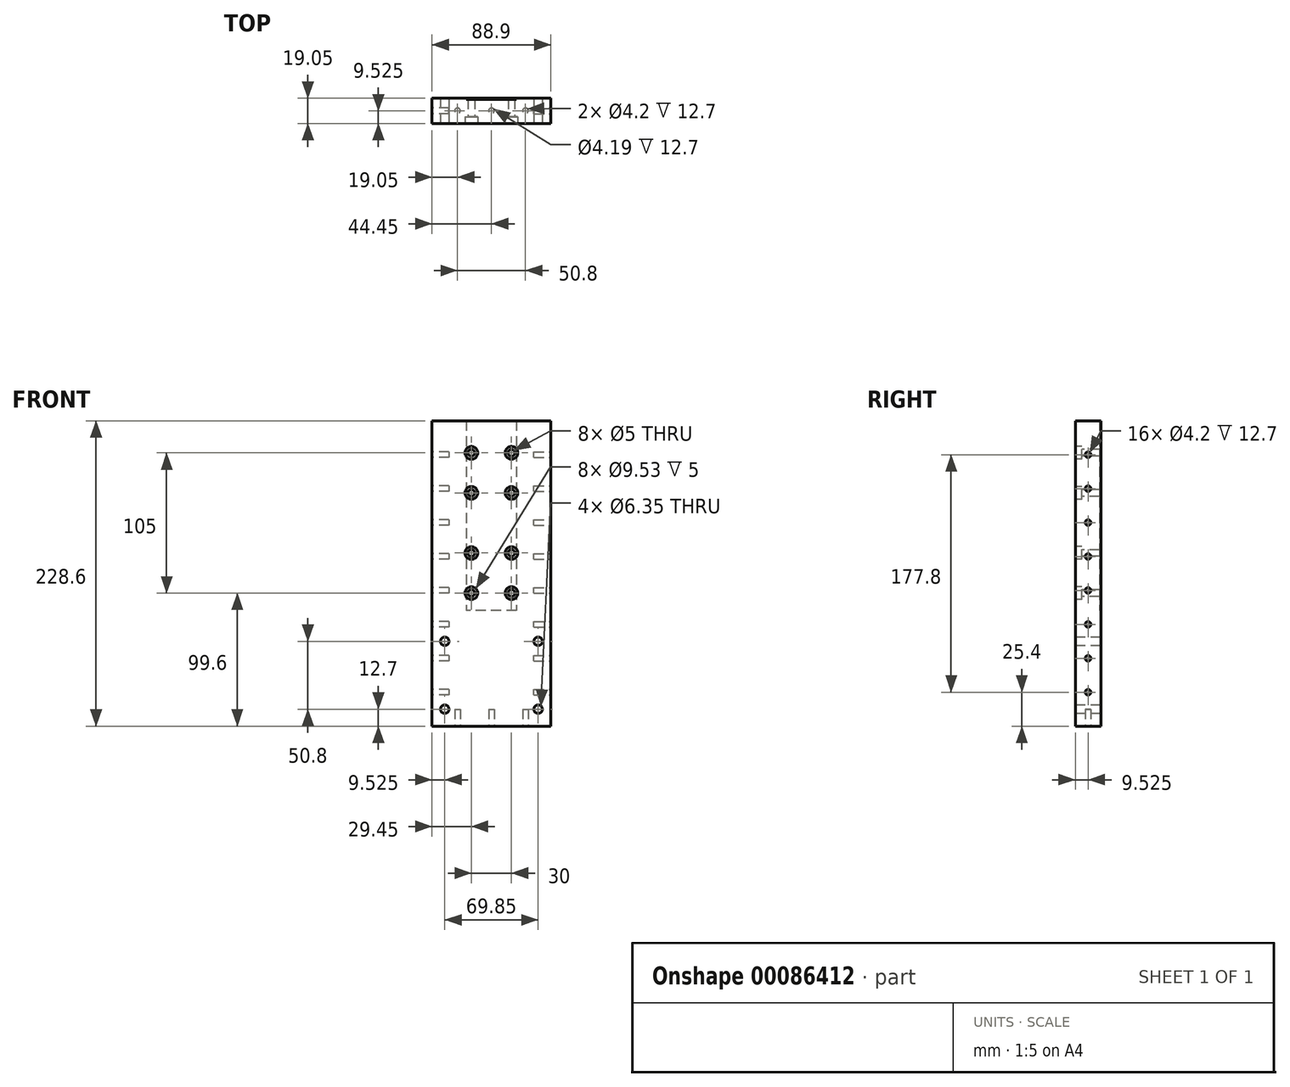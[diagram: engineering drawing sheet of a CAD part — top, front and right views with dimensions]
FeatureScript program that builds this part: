
annotation { "Feature Type Name" : "Feature", "Feature Type Description" : "" }
export const myFeature = defineFeature(function(context is Context, id is Id, definition is map)
    precondition{}
    {
        {
            var Q0;
            Q0=qCreatedBy(makeId("Front.planeOp"),FACE);
            var sketch = newSketch(context, id + "F0", { "sketchPlane" : qUnion([Q0])});
            skLineSegment(sketch, "E0.bottom", {"start": v(44.45, -114.3) * mm, "end": v(-44.45, -114.3) * mm});
            skLineSegment(sketch, "E0.top", {"start": v(44.45, 114.3) * mm, "end": v(-44.45, 114.3) * mm});
            skLineSegment(sketch, "E0.left", {"start": v(44.45, -114.3) * mm, "end": v(44.45, 114.3) * mm});
            skLineSegment(sketch, "E0.right", {"start": v(-44.45, -114.3) * mm, "end": v(-44.45, 114.3) * mm});
            skPoint(sketch, "E0.middle", {"position": v(0, 0) * mm});
            skSolve(sketch);
        }
        {
            var Q0;
            Q0=makeQuery(id+"F0.imprint","IMPRINT",FACE,{"disambiguationData":[TD([[makeQuery(id+"F0.imprint","IMPRINT",EDGE,{"derivedFrom":sQuery(id+"F0.wireOp",EDGE,"E0.bottom")}),-1.0]])]});
            extrude(context, id + "F1", {"entities" : qUnion([Q0]), "oppositeDirection" : true, "depth" : 19.05 * mm});
        }
        {
            var Q0;
            Q0=makeQuery(id+"F1.opExtrude","CAP_FACE",FACE,{"disambiguationData":[OSD([sQuery(id+"F0.wireOp",EDGE,"E0.bottom"),sQuery(id+"F0.wireOp",EDGE,"E0.top"),sQuery(id+"F0.wireOp",EDGE,"E0.left"),sQuery(id+"F0.wireOp",EDGE,"E0.right")])],"isStart":true});
            var sketch = newSketch(context, id + "F2", { "sketchPlane" : qUnion([Q0])});
            skLineSegment(sketch, "E1", {"start": v(0, 118.6) * mm, "end": v(0, -123.74) * mm, "construction": true});
            skPoint(sketch, "E1.endSnap0", {"position": v(0, -114.3) * mm});
            skLineSegment(sketch, "E2", {"start": v(-15, 118.28) * mm, "end": v(-15, -54.2) * mm, "construction": true});
            skLineSegment(sketch, "E3", {"start": v(15, 118.28) * mm, "end": v(15, -54.75) * mm, "construction": true});
            skLineSegment(sketch, "E4", {"start": v(-47, 90.3) * mm, "end": v(45.55, 90.3) * mm});
            skLineSegment(sketch, "E5", {"start": v(-45.9, 60.3) * mm, "end": v(47.2, 60.3) * mm});
            skLineSegment(sketch, "E6", {"start": v(-45.9, 15.3) * mm, "end": v(49.67, 15.3) * mm});
            skLineSegment(sketch, "E7", {"start": v(-46.73, -14.7) * mm, "end": v(49.4, -14.7) * mm});
            skCircle(sketch, "E8", {"center": v(-15, 90.3) * mm, "radius": 2.5 * mm});
            skCircle(sketch, "E9", {"center": v(15, 90.3) * mm, "radius": 2.5 * mm});
            skCircle(sketch, "E10", {"center": v(-15, 60.3) * mm, "radius": 2.5 * mm});
            skCircle(sketch, "E11", {"center": v(15, 60.3) * mm, "radius": 2.5 * mm});
            skCircle(sketch, "E12", {"center": v(-15, 15.3) * mm, "radius": 2.5 * mm});
            skCircle(sketch, "E13", {"center": v(15, 15.3) * mm, "radius": 2.5 * mm});
            skCircle(sketch, "E14", {"center": v(-15, -14.7) * mm, "radius": 2.5 * mm});
            skCircle(sketch, "E15", {"center": v(15, -14.7) * mm, "radius": 2.5 * mm});
            skSolve(sketch);
        }
        {
            var Q0;
            Q0 = qSketchRegion(id + "F2", true);
            extrude(context, id + "F3", {"entities" : qUnion([Q0]), "operationType" : NewBodyOperationType.REMOVE, "endBound" : BoundingType.THROUGH_ALL, "oppositeDirection" : true, "depth" : 25.4 * mm});
        }
        {
            var Q0;
            Q0=makeQuery(id+"F1.opExtrude","CAP_FACE",FACE,{"disambiguationData":[OSD([sQuery(id+"F0.wireOp",EDGE,"E0.bottom"),sQuery(id+"F0.wireOp",EDGE,"E0.top"),sQuery(id+"F0.wireOp",EDGE,"E0.left"),sQuery(id+"F0.wireOp",EDGE,"E0.right")])],"isStart":true});
            var sketch = newSketch(context, id + "F4", { "sketchPlane" : qUnion([Q0])});
            skCircle(sketch, "E16", {"center": v(-15, -14.7) * mm, "radius": 4.76 * mm});
            skCircle(sketch, "E17", {"center": v(15, -14.7) * mm, "radius": 4.76 * mm});
            skCircle(sketch, "E18", {"center": v(15, 15.3) * mm, "radius": 4.76 * mm});
            skCircle(sketch, "E19", {"center": v(-15, 15.3) * mm, "radius": 4.76 * mm});
            skCircle(sketch, "E20", {"center": v(-15, 60.3) * mm, "radius": 4.76 * mm});
            skCircle(sketch, "E21", {"center": v(15, 60.3) * mm, "radius": 4.76 * mm});
            skCircle(sketch, "E22", {"center": v(-15, 90.3) * mm, "radius": 4.76 * mm});
            skCircle(sketch, "E23", {"center": v(15, 90.3) * mm, "radius": 4.76 * mm});
            skSolve(sketch);
        }
        {
            var Q0;
            Q0 = qSketchRegion(id + "F4", true);
            extrude(context, id + "F5", {"entities" : qUnion([Q0]), "operationType" : NewBodyOperationType.REMOVE, "oppositeDirection" : true, "depth" : 5 * mm});
        }
        {
            var Q0;
            Q0=makeQuery(id+"F1.opExtrude","SWEPT_FACE",FACE,{"disambiguationData":[OSD([sQuery(id+"F0.wireOp",EDGE,"E0.right")])]});
            var sketch = newSketch(context, id + "F6", { "sketchPlane" : qUnion([Q0])});
            skLineSegment(sketch, "E24", {"start": v(-9.53, -118.31) * mm, "end": v(-9.53, 120.01) * mm, "construction": true});
            skPoint(sketch, "E24.startSnap0", {"position": v(-9.53, -114.3) * mm});
            skCircle(sketch, "E25", {"center": v(-9.53, 88.9) * mm, "radius": 2.1 * mm});
            skCircle(sketch, "E26", {"center": v(-9.53, 63.5) * mm, "radius": 2.1 * mm});
            skCircle(sketch, "E27", {"center": v(-9.53, 38.1) * mm, "radius": 2.1 * mm});
            skCircle(sketch, "E28", {"center": v(-9.53, 12.7) * mm, "radius": 2.1 * mm});
            skCircle(sketch, "E29", {"center": v(-9.53, -12.7) * mm, "radius": 2.1 * mm});
            skCircle(sketch, "E30", {"center": v(-9.53, -38.1) * mm, "radius": 2.1 * mm});
            skCircle(sketch, "E31", {"center": v(-9.52, -63.5) * mm, "radius": 2.1 * mm});
            skCircle(sketch, "E32", {"center": v(-9.52, -88.9) * mm, "radius": 2.1 * mm});
            skSolve(sketch);
        }
        {
            var Q0;
            Q0 = qSketchRegion(id + "F6", true);
            extrude(context, id + "F7", {"entities" : qUnion([Q0]), "operationType" : NewBodyOperationType.REMOVE, "oppositeDirection" : true, "depth" : 12.7 * mm});
        }
        {
            var Q0;
            Q0=makeQuery(id+"F1.opExtrude","SWEPT_FACE",FACE,{"disambiguationData":[OSD([sQuery(id+"F0.wireOp",EDGE,"E0.left")])]});
            var sketch = newSketch(context, id + "F8", { "sketchPlane" : qUnion([Q0])});
            skLineSegment(sketch, "E33", {"start": v(9.53, 119.45) * mm, "end": v(9.53, -118.31) * mm, "construction": true});
            skPoint(sketch, "E33.startSnap0", {"position": v(9.53, 114.3) * mm});
            skCircle(sketch, "E34", {"center": v(9.53, 88.9) * mm, "radius": 2.1 * mm});
            skCircle(sketch, "E35", {"center": v(9.53, 63.5) * mm, "radius": 2.1 * mm});
            skCircle(sketch, "E36", {"center": v(9.53, 38.1) * mm, "radius": 2.1 * mm});
            skCircle(sketch, "E37", {"center": v(9.53, 12.7) * mm, "radius": 2.1 * mm});
            skCircle(sketch, "E38", {"center": v(9.53, -63.5) * mm, "radius": 2.1 * mm});
            skCircle(sketch, "E39", {"center": v(9.53, -12.7) * mm, "radius": 2.1 * mm});
            skCircle(sketch, "E40", {"center": v(9.53, -38.1) * mm, "radius": 2.1 * mm});
            skCircle(sketch, "E41", {"center": v(9.53, -88.9) * mm, "radius": 2.1 * mm});
            skSolve(sketch);
        }
        {
            var Q0;
            Q0 = qSketchRegion(id + "F8", true);
            extrude(context, id + "F9", {"entities" : qUnion([Q0]), "operationType" : NewBodyOperationType.REMOVE, "oppositeDirection" : true, "depth" : 12.7 * mm});
        }
        {
            var Q0;
            Q0=makeQuery(id+"F1.opExtrude","SWEPT_FACE",FACE,{"disambiguationData":[OSD([sQuery(id+"F0.wireOp",EDGE,"E0.bottom")])]});
            var sketch = newSketch(context, id + "F10", { "sketchPlane" : qUnion([Q0])});
            skLineSegment(sketch, "E42", {"start": v(-44.31, -9.53) * mm, "end": v(50.75, -9.52) * mm, "construction": true});
            skCircle(sketch, "E43", {"center": v(-25.4, -9.53) * mm, "radius": 2.1 * mm});
            skCircle(sketch, "E44", {"center": v(25.4, -9.53) * mm, "radius": 2.1 * mm});
            skCircle(sketch, "E45", {"center": v(0, -9.53) * mm, "radius": 2.1 * mm});
            skSolve(sketch);
        }
        {
            var Q0;
            Q0 = qSketchRegion(id + "F10", true);
            extrude(context, id + "F11", {"entities" : qUnion([Q0]), "operationType" : NewBodyOperationType.REMOVE, "oppositeDirection" : true, "depth" : 12.7 * mm});
        }
        {
            var Q0;
            Q0=makeQuery(id+"F1.opExtrude","CAP_FACE",FACE,{"disambiguationData":[OSD([sQuery(id+"F0.wireOp",EDGE,"E0.bottom"),sQuery(id+"F0.wireOp",EDGE,"E0.top"),sQuery(id+"F0.wireOp",EDGE,"E0.left"),sQuery(id+"F0.wireOp",EDGE,"E0.right")])],"isStart":false});
            var sketch = newSketch(context, id + "F12", { "sketchPlane" : qUnion([Q0])});
            skLineSegment(sketch, "E46.bottom", {"start": v(-18.75, 114.3) * mm, "end": v(18.75, 114.3) * mm});
            skLineSegment(sketch, "E46.top", {"start": v(-18.75, -27.7) * mm, "end": v(18.75, -27.7) * mm});
            skLineSegment(sketch, "E46.left", {"start": v(-18.75, 114.3) * mm, "end": v(-18.75, -27.7) * mm});
            skLineSegment(sketch, "E46.right", {"start": v(18.75, 114.3) * mm, "end": v(18.75, -27.7) * mm});
            skSolve(sketch);
        }
        {
            var Q0;
            Q0 = qSketchRegion(id + "F12", true);
            extrude(context, id + "F13", {"entities" : qUnion([Q0]), "operationType" : NewBodyOperationType.REMOVE, "oppositeDirection" : true, "depth" : 0.89 * mm});
        }
        {
            var Q0;
            Q0=makeQuery(id+"F1.opExtrude","CAP_FACE",FACE,{"disambiguationData":[OSD([sQuery(id+"F0.wireOp",EDGE,"E0.bottom"),sQuery(id+"F0.wireOp",EDGE,"E0.top"),sQuery(id+"F0.wireOp",EDGE,"E0.left"),sQuery(id+"F0.wireOp",EDGE,"E0.right")])],"isStart":true});
            var sketch = newSketch(context, id + "F14", { "sketchPlane" : qUnion([Q0])});
            skLineSegment(sketch, "E47", {"start": v(-67.46, -101.6) * mm, "end": v(67.04, -101.6) * mm, "construction": true});
            skLineSegment(sketch, "E48", {"start": v(-67.04, -50.8) * mm, "end": v(65.8, -50.8) * mm, "construction": true});
            skLineSegment(sketch, "E49", {"start": v(-34.93, -39.4) * mm, "end": v(-34.92, -120.58) * mm, "construction": true});
            skLineSegment(sketch, "E50", {"start": v(34.93, -39.8) * mm, "end": v(34.93, -121.38) * mm, "construction": true});
            skLineSegment(sketch, "E51", {"start": v(0, 0) * mm, "end": v(0, -125.37) * mm, "construction": true});
            skPoint(sketch, "E51.endSnap0", {"position": v(0, -114.3) * mm});
            skCircle(sketch, "E52", {"center": v(-34.93, -50.8) * mm, "radius": 3.18 * mm});
            skCircle(sketch, "E53", {"center": v(-34.93, -101.6) * mm, "radius": 3.18 * mm});
            skCircle(sketch, "E54", {"center": v(34.93, -50.8) * mm, "radius": 3.18 * mm});
            skCircle(sketch, "E55", {"center": v(34.93, -101.6) * mm, "radius": 3.18 * mm});
            skSolve(sketch);
        }
        {
            var Q0;
            Q0 = qSketchRegion(id + "F14", true);
            extrude(context, id + "F15", {"entities" : qUnion([Q0]), "operationType" : NewBodyOperationType.REMOVE, "endBound" : BoundingType.THROUGH_ALL, "oppositeDirection" : true, "depth" : 25.4 * mm});
        }
    });
